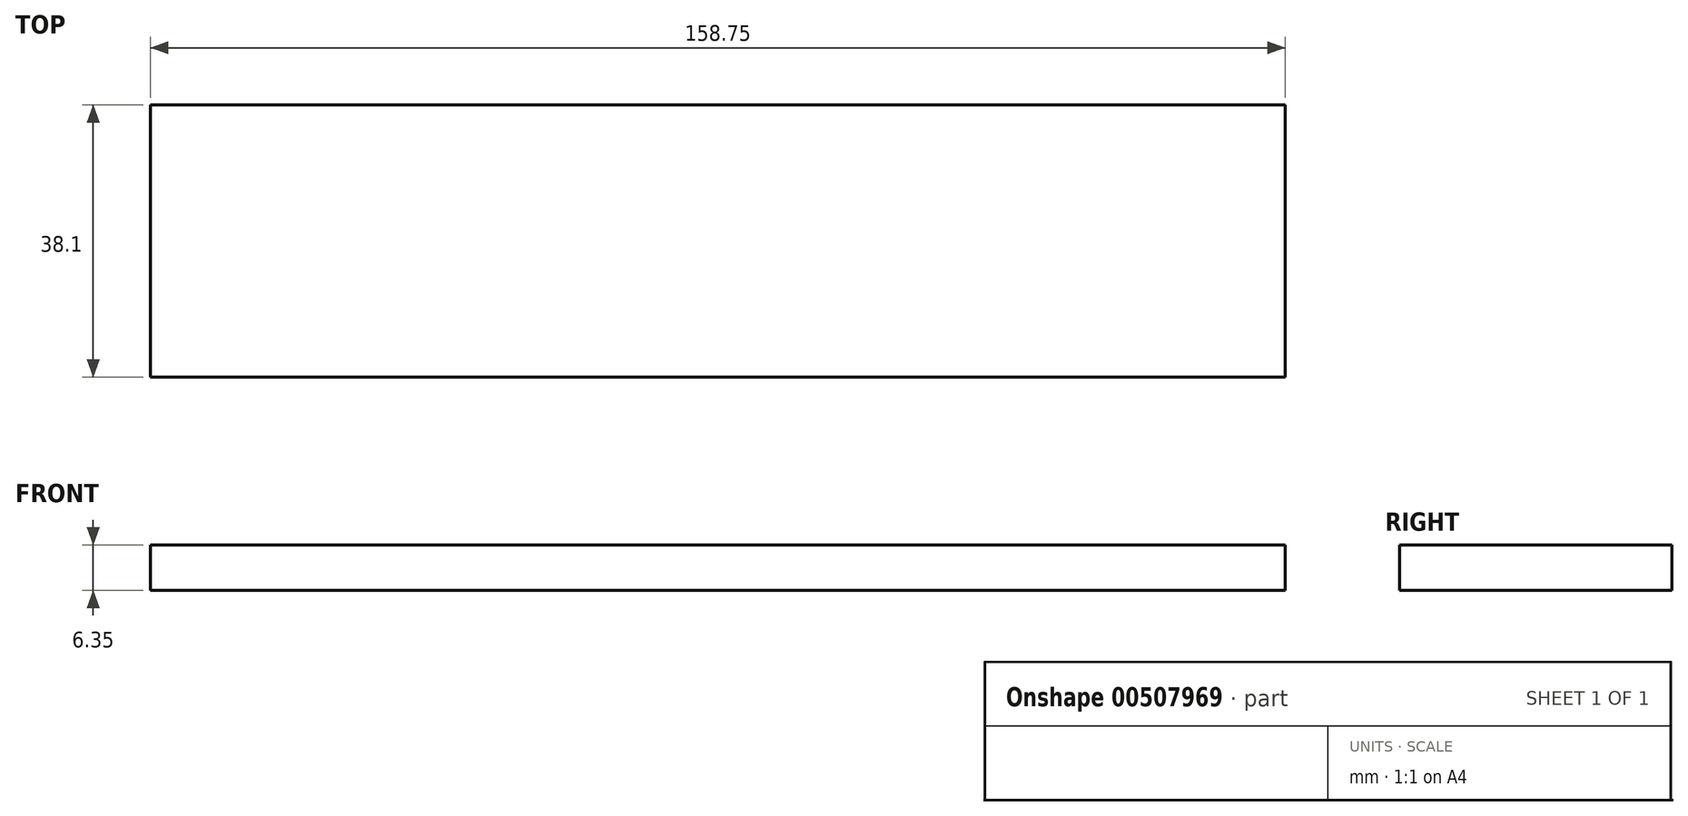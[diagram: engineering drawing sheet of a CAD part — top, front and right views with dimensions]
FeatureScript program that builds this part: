
annotation { "Feature Type Name" : "Feature", "Feature Type Description" : "" }
export const myFeature = defineFeature(function(context is Context, id is Id, definition is map)
    precondition{}
    {
        {
            var Q0;
            Q0=qCreatedBy(makeId("Top.planeOp"),FACE);
            var sketch = newSketch(context, id + "F0", { "sketchPlane" : qUnion([Q0])});
            skLineSegment(sketch, "E0.bottom", {"start": v(0, 0) * mm, "end": v(158.75, 0) * mm});
            skLineSegment(sketch, "E0.top", {"start": v(0, -38.1) * mm, "end": v(158.75, -38.1) * mm});
            skLineSegment(sketch, "E0.left", {"start": v(0, 0) * mm, "end": v(0, -38.1) * mm});
            skLineSegment(sketch, "E0.right", {"start": v(158.75, 0) * mm, "end": v(158.75, -38.1) * mm});
            skSolve(sketch);
        }
        {
            var Q0;
            Q0=makeQuery(id+"F0.imprint","IMPRINT",FACE,{"disambiguationData":[TD([[makeQuery(id+"F0.imprint","IMPRINT",EDGE,{"derivedFrom":sQuery(id+"F0.wireOp",EDGE,"E0.bottom")}),-1.0]])]});
            extrude(context, id + "F1", {"entities" : qUnion([Q0]), "depth" : 6.35 * mm, "offsetDistance" : 25.4 * mm});
        }
    });
